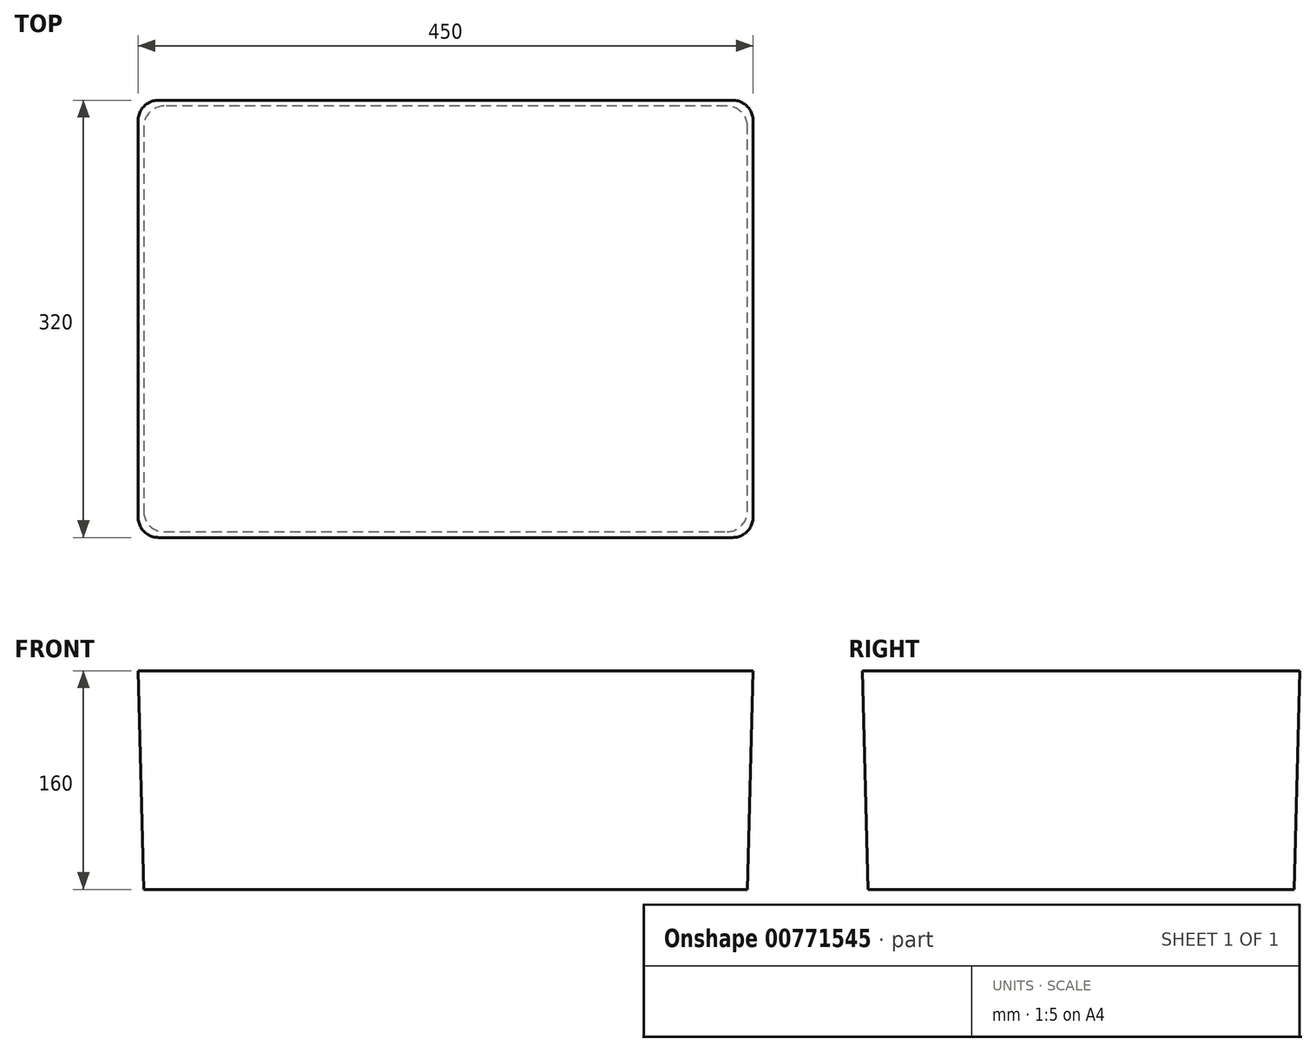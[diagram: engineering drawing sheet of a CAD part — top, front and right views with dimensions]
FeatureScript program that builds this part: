
annotation { "Feature Type Name" : "Feature", "Feature Type Description" : "" }
export const myFeature = defineFeature(function(context is Context, id is Id, definition is map)
    precondition{}
    {
        {
            var Q0;
            Q0=qCreatedBy(makeId("Top.planeOp"),FACE);
            var sketch = newSketch(context, id + "F0", { "sketchPlane" : qUnion([Q0])});
            skLineSegment(sketch, "E0.bottom", {"start": v(225, 160) * mm, "end": v(-225, 160) * mm});
            skLineSegment(sketch, "E0.top", {"start": v(225, -160) * mm, "end": v(-225, -160) * mm});
            skLineSegment(sketch, "E0.left", {"start": v(225, 160) * mm, "end": v(225, -160) * mm});
            skLineSegment(sketch, "E0.right", {"start": v(-225, 160) * mm, "end": v(-225, -160) * mm});
            skPoint(sketch, "E0.middle", {"position": v(0, 0) * mm});
            skSolve(sketch);
        }
        {
            var Q0;
            Q0=makeQuery(id+"F0.imprint","IMPRINT",FACE,{"disambiguationData":[TD([[makeQuery(id+"F0.imprint","IMPRINT",EDGE,{"derivedFrom":sQuery(id+"F0.wireOp",EDGE,"E0.bottom")}),1.0]])]});
            extrude(context, id + "F1", {"entities" : qUnion([Q0]), "oppositeDirection" : true, "depth" : 160 * mm, "offsetDistance" : 25 * mm, "hasDraft" : true, "draftAngle" : 1.5 * degree, "draftPullDirection" : true});
        }
        {
            var Q0;
            Q0=makeQuery(id+"F1.opExtrude","SWEPT_EDGE",EDGE,{"disambiguationData":[OSD([sQuery(id+"F0.wireOp",EDGE,"E0.bottom"),sQuery(id+"F0.wireOp",EDGE,"E0.right")])]});
            var Q1;
            Q1=makeQuery(id+"F1.opExtrude","SWEPT_EDGE",EDGE,{"disambiguationData":[OSD([sQuery(id+"F0.wireOp",EDGE,"E0.top"),sQuery(id+"F0.wireOp",EDGE,"E0.right")])]});
            var Q2;
            Q2=makeQuery(id+"F1.opExtrude","SWEPT_EDGE",EDGE,{"disambiguationData":[OSD([sQuery(id+"F0.wireOp",EDGE,"E0.top"),sQuery(id+"F0.wireOp",EDGE,"E0.left")])]});
            var Q3;
            Q3=makeQuery(id+"F1.opExtrude","SWEPT_EDGE",EDGE,{"disambiguationData":[OSD([sQuery(id+"F0.wireOp",EDGE,"E0.bottom"),sQuery(id+"F0.wireOp",EDGE,"E0.left")])]});
            fillet(context, id + "F2", {"entities" : qUnion([Q0, Q1, Q2, Q3]), "radius" : 15 * mm, "tangentPropagation" : true, "allowEdgeOverflow" : false});
        }
    });
